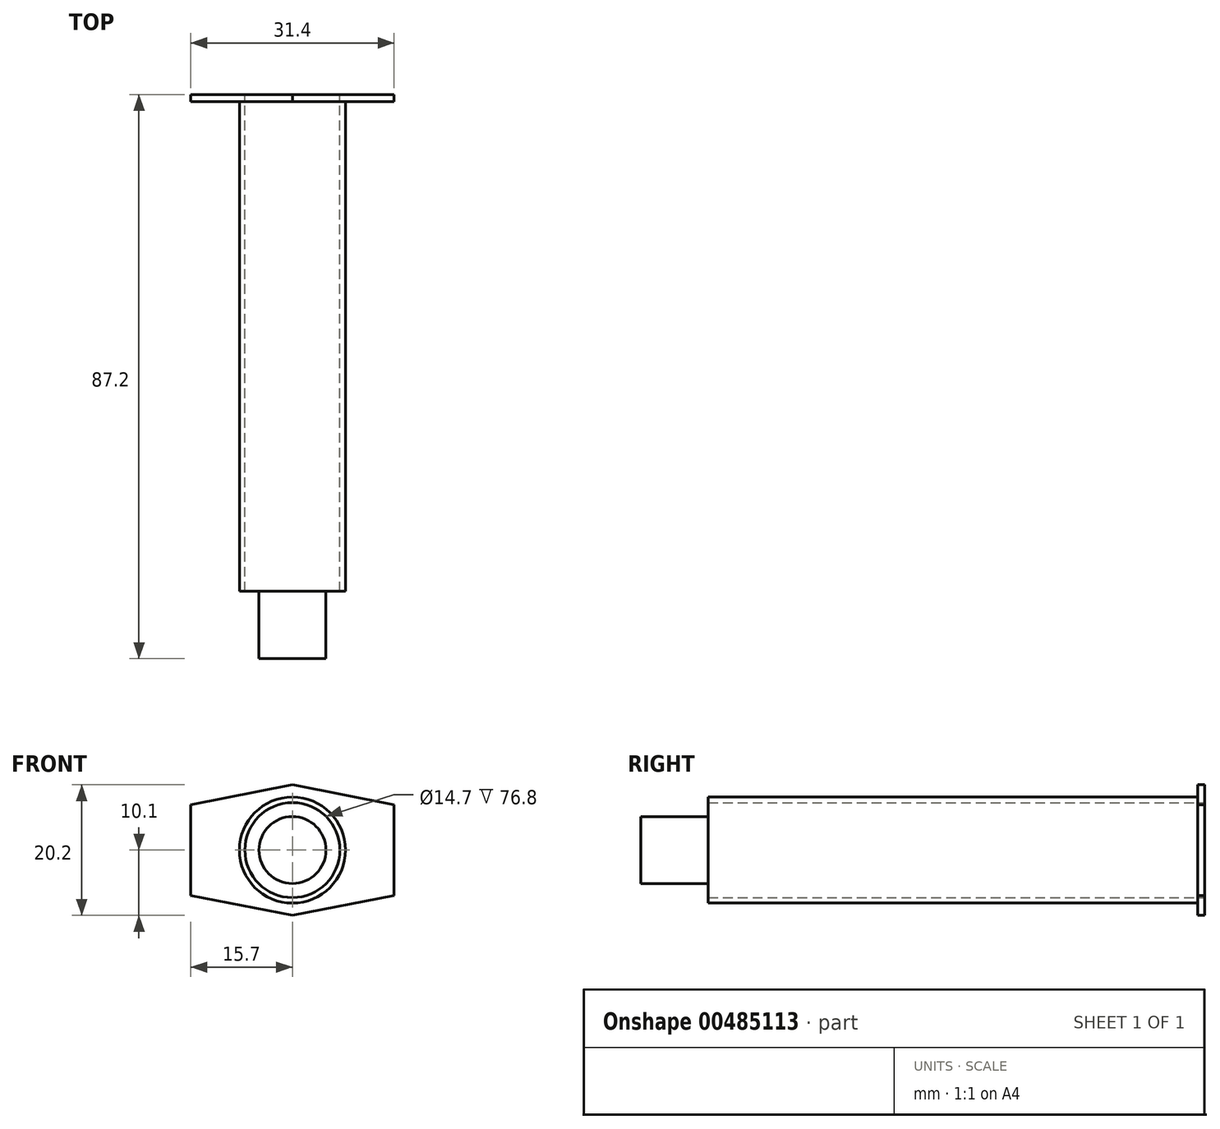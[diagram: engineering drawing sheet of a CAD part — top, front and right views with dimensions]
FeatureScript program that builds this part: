
annotation { "Feature Type Name" : "Feature", "Feature Type Description" : "" }
export const myFeature = defineFeature(function(context is Context, id is Id, definition is map)
    precondition{}
    {
        {
            var Q0;
            Q0=qCreatedBy(makeId("Front.planeOp"),FACE);
            var sketch = newSketch(context, id + "F0", { "sketchPlane" : qUnion([Q0])});
            skLineSegment(sketch, "E0.bottom", {"start": v(-15.7, -10.1) * mm, "end": v(15.7, -10.1) * mm, "construction": true});
            skLineSegment(sketch, "E0.top", {"start": v(-15.7, 10.1) * mm, "end": v(15.7, 10.1) * mm, "construction": true});
            skLineSegment(sketch, "E0.left", {"start": v(-15.7, -10.1) * mm, "end": v(-15.7, 10.1) * mm, "construction": true});
            skLineSegment(sketch, "E0.right", {"start": v(15.7, -10.1) * mm, "end": v(15.7, 10.1) * mm, "construction": true});
            skPoint(sketch, "E0.middle", {"position": v(0, 0) * mm});
            skLineSegment(sketch, "E1", {"start": v(-15.7, 7) * mm, "end": v(15.7, 7) * mm, "construction": true});
            skLineSegment(sketch, "E2", {"start": v(-15.7, -7) * mm, "end": v(15.7, -7) * mm, "construction": true});
            skLineSegment(sketch, "E3", {"start": v(0, 10.1) * mm, "end": v(15.7, 7) * mm});
            skLineSegment(sketch, "E4", {"start": v(15.7, -7) * mm, "end": v(0, -10.1) * mm});
            skLineSegment(sketch, "E5", {"start": v(0, -10.1) * mm, "end": v(-15.7, -7) * mm});
            skLineSegment(sketch, "E6", {"start": v(-15.7, 7) * mm, "end": v(0, 10.1) * mm});
            skLineSegment(sketch, "E7", {"start": v(-15.7, -7) * mm, "end": v(-15.7, 7) * mm});
            skLineSegment(sketch, "E8", {"start": v(15.7, 7) * mm, "end": v(15.7, -7) * mm});
            skCircle(sketch, "E9", {"center": v(0, 0) * mm, "radius": 7.35 * mm});
            skCircle(sketch, "E10", {"center": v(0, 0) * mm, "radius": 8.2 * mm});
            skSolve(sketch);
        }
        {
            var Q0;
            Q0=makeQuery(id+"F0.imprint","IMPRINT",FACE,{"disambiguationData":[TD([[makeQuery(id+"F0.imprint","IMPRINT",EDGE,{"derivedFrom":sQuery(id+"F0.wireOp",EDGE,"E9")}),-1.0]])]});
            extrude(context, id + "F1", {"entities" : qUnion([Q0]), "depth" : 76.8 * mm});
        }
        {
            var Q0;
            Q0=makeQuery(id+"F0.imprint","IMPRINT",FACE,{"disambiguationData":[TD([[makeQuery(id+"F0.imprint","IMPRINT",EDGE,{"derivedFrom":sQuery(id+"F0.wireOp",EDGE,"E3")}),-1.0]])]});
            extrude(context, id + "F2", {"entities" : qUnion([Q0]), "operationType" : NewBodyOperationType.ADD, "depth" : 1.1 * mm});
        }
        {
            var Q0;
            Q0=makeQuery(id+"F1.opExtrude","CAP_FACE",FACE,{"disambiguationData":[OSD([sQuery(id+"F0.wireOp",EDGE,"E9"),sQuery(id+"F0.wireOp",EDGE,"E10")])],"isStart":false});
            var sketch = newSketch(context, id + "F3", { "sketchPlane" : qUnion([Q0])});
            skCircle(sketch, "E11", {"center": v(0, 0) * mm, "radius": 5.18 * mm});
            skSolve(sketch);
        }
        {
            var Q0;
            Q0=makeQuery(id+"F3.imprint","IMPRINT",FACE,{"disambiguationData":[TD([[makeQuery(id+"F3.imprint","IMPRINT",EDGE,{"derivedFrom":sQuery(id+"F3.wireOp",EDGE,"E11")}),1.0]])]});
            extrude(context, id + "F4", {"entities" : qUnion([Q0]), "depth" : 10.4 * mm});
        }
    });
